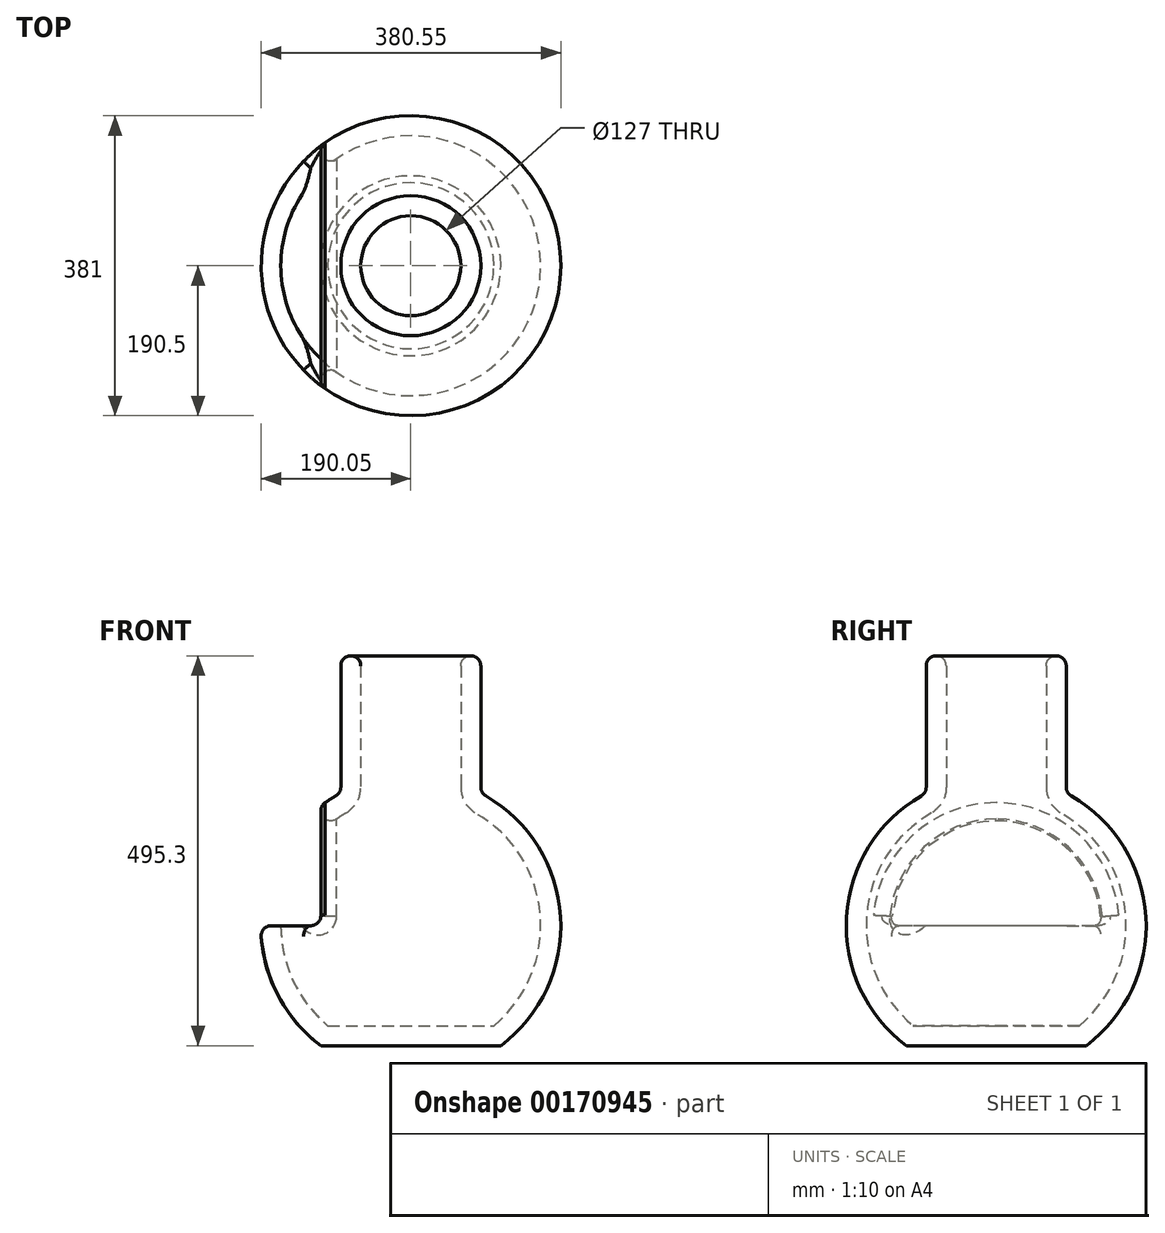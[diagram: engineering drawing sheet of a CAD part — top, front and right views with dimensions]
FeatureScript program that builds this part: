
annotation { "Feature Type Name" : "Feature", "Feature Type Description" : "" }
export const myFeature = defineFeature(function(context is Context, id is Id, definition is map)
    precondition{}
    {
        {
            var Q0;
            Q0=qCreatedBy(makeId("Front.planeOp"),FACE);
            var sketch = newSketch(context, id + "F0", { "sketchPlane" : qUnion([Q0])});
            skArc(sketch, "E0", {"start": v(-95.25, 164.98) * mm, "mid": v(-190.16, 11.41) * mm, "end": v(-114.3, -152.4) * mm});
            skLineSegment(sketch, "E1", {"start": v(0, -152.4) * mm, "end": v(0, 342.9) * mm});
            skLineSegment(sketch, "E2", {"start": v(0, 0) * mm, "end": v(-190.5, 0) * mm});
            skLineSegment(sketch, "E3", {"start": v(0, 342.9) * mm, "end": v(-88.9, 342.9) * mm});
            skLineSegment(sketch, "E4", {"start": v(-88.9, 342.9) * mm, "end": v(-88.9, 175.98) * mm});
            skLineSegment(sketch, "E5", {"start": v(-174.6, -76.2) * mm, "end": v(0, -76.2) * mm});
            skLineSegment(sketch, "E6", {"start": v(0, -152.4) * mm, "end": v(-114.3, -152.4) * mm});
            skLineSegment(sketch, "E7", {"start": v(-174.6, 76.2) * mm, "end": v(0, 76.2) * mm});
            skLineSegment(sketch, "E8", {"start": v(0, 152.4) * mm, "end": v(-114.3, 152.4) * mm});
            skLineSegment(sketch, "E9", {"start": v(-114.3, 152.4) * mm, "end": v(-114.3, 0) * mm});
            skPoint(sketch, "E10.newPointB", {"position": v(0, 190.5) * mm});
            skArc(sketch, "E10.filletArc", {"start": v(-95.25, 164.98) * mm, "mid": v(-90.6, 169.63) * mm, "end": v(-88.9, 175.98) * mm});
            skSolve(sketch);
        }
        {
            var Q0;
            {var subQ4=sQuery(id+"F0.wireOp",EDGE,"E3");Q0=makeQuery(id+"F0.imprint","IMPRINT",FACE,{"disambiguationData":[TD([[makeQuery(id+"F0.imprint","IMPRINT",EDGE,{"derivedFrom":subQ4}),1.0]])]});}
            var Q1;
            {var subQ4=sQuery(id+"F0.wireOp",EDGE,"E8");Q1=makeQuery(id+"F0.imprint","IMPRINT",FACE,{"disambiguationData":[TD([[makeQuery(id+"F0.imprint","IMPRINT",EDGE,{"derivedFrom":subQ4}),-1.0]])]});}
            var Q2;
            {var subQ3=sQuery(id+"F0.wireOp",EDGE,"E8");Q2=makeQuery(id+"F0.imprint","IMPRINT",FACE,{"disambiguationData":[TD([[makeQuery(id+"F0.imprint","IMPRINT",EDGE,{"derivedFrom":subQ3}),1.0]])]});}
            var Q3;
            {var subQ0=sQuery(id+"F0.wireOp",EDGE,"E7");var subQ1=sQuery(id+"F0.wireOp",EDGE,"E0");var subQ2=makeQuery(id+"F0.imprint","INTERSECT",VERTEX,{"derivedFrom":[subQ1,subQ0]});Q3=makeQuery(id+"F0.imprint","IMPRINT",FACE,{"disambiguationData":[TD([[makeQuery(id+"F0.imprint","IMPRINT",EDGE,{"disambiguationData":[TD([[subQ2,-1.0]])],"derivedFrom":subQ0}),1.0]])]});}
            var Q4;
            {var subQ0=sQuery(id+"F0.wireOp",EDGE,"E2");var subQ1=sQuery(id+"F0.wireOp",EDGE,"E0");var subQ2=makeQuery(id+"F0.imprint","INTERSECT",VERTEX,{"derivedFrom":[subQ1,subQ0]});Q4=makeQuery(id+"F0.imprint","IMPRINT",FACE,{"disambiguationData":[TD([[makeQuery(id+"F0.imprint","IMPRINT",EDGE,{"disambiguationData":[TD([[subQ2,1.0]])],"derivedFrom":subQ1}),1.0]])]});}
            var Q5;
            {var subQ0=sQuery(id+"F0.wireOp",EDGE,"E2");var subQ1=sQuery(id+"F0.wireOp",EDGE,"E1");var subQ2=makeQuery(id+"F0.imprint","INTERSECT",VERTEX,{"derivedFrom":[subQ1,subQ0]});Q5=makeQuery(id+"F0.imprint","IMPRINT",FACE,{"disambiguationData":[TD([[makeQuery(id+"F0.imprint","IMPRINT",EDGE,{"disambiguationData":[TD([[subQ2,-1.0]])],"derivedFrom":subQ1}),1.0]])]});}
            var Q6;
            {var subQ6=sQuery(id+"F0.wireOp",EDGE,"E5");Q6=makeQuery(id+"F0.imprint","IMPRINT",FACE,{"disambiguationData":[TD([[makeQuery(id+"F0.imprint","IMPRINT",EDGE,{"derivedFrom":subQ6}),1.0]])]});}
            var Q7;
            {var subQ0=sQuery(id+"F0.wireOp",EDGE,"E5");Q7=makeQuery(id+"F0.imprint","IMPRINT",FACE,{"disambiguationData":[TD([[makeQuery(id+"F0.imprint","IMPRINT",EDGE,{"derivedFrom":subQ0}),-1.0]])]});}
            var Q8;
            Q8=sQuery(id+"F0.wireOp",EDGE,"E1");
            revolve(context, id + "F1", {"entities" : qUnion([Q0, Q1, Q2, Q3, Q4, Q5, Q6, Q7]), "axis" : qUnion([Q8]), "revolveType" : RevolveType.FULL});
        }
        {
            var Q0;
            Q0=makeQuery(id+"F1.opRevolve","SWEPT_FACE",FACE,{"disambiguationData":[OSD([sQuery(id+"F0.wireOp",EDGE,"E3")])]});
            shell(context, id + "F2", {"entities" : qUnion([Q0]), "thickness" : 25.4 * mm});
        }
        {
            var Q0;
            Q0=makeQuery(id+"F1.opRevolve","SWEPT_FACE",FACE,{"disambiguationData":[OSD([sQuery(id+"F0.wireOp",EDGE,"E3")])]});
            fillet(context, id + "F3", {"entities" : qUnion([Q0]), "radius" : 12.7 * mm, "tangentPropagation" : true, "allowEdgeOverflow" : false});
        }
        {
            var Q0;
            {var subQ0=sQuery(id+"F0.wireOp",EDGE,"E7");var subQ1=sQuery(id+"F0.wireOp",EDGE,"E0");var subQ2=makeQuery(id+"F0.imprint","INTERSECT",VERTEX,{"derivedFrom":[subQ1,subQ0]});Q0=makeQuery(id+"F0.imprint","IMPRINT",FACE,{"disambiguationData":[TD([[makeQuery(id+"F0.imprint","IMPRINT",EDGE,{"disambiguationData":[TD([[subQ2,-1.0]])],"derivedFrom":subQ0}),1.0]])]});}
            var Q1;
            {var subQ0=sQuery(id+"F0.wireOp",EDGE,"E2");var subQ1=sQuery(id+"F0.wireOp",EDGE,"E0");var subQ2=makeQuery(id+"F0.imprint","INTERSECT",VERTEX,{"derivedFrom":[subQ1,subQ0]});Q1=makeQuery(id+"F0.imprint","IMPRINT",FACE,{"disambiguationData":[TD([[makeQuery(id+"F0.imprint","IMPRINT",EDGE,{"disambiguationData":[TD([[subQ2,1.0]])],"derivedFrom":subQ1}),1.0]])]});}
            extrude(context, id + "F4", {"entities" : qUnion([Q0, Q1]), "operationType" : NewBodyOperationType.REMOVE, "endBound" : BoundingType.THROUGH_ALL, "oppositeDirection" : true, "depth" : 25.4 * mm, "hasSecondDirection" : true, "secondDirectionOppositeDirection" : false, "secondDirectionDepth" : 181.6 * mm});
        }
        {
            var Q0;
            Q0=makeQuery(id+"F4.boolean.opBoolean","INTERSECT",EDGE,{"derivedFrom":[makeQuery(id+"F1.opRevolve","SWEPT_FACE",FACE,{"disambiguationData":[OSD([sQuery(id+"F0.wireOp",EDGE,"E0")])]}),makeQuery(id+"F4.opExtrude","SWEPT_FACE",FACE,{"disambiguationData":[OSD([sQuery(id+"F0.wireOp",EDGE,"E2")])]})]});
            fillet(context, id + "F5", {"entities" : qUnion([Q0]), "radius" : 12.7 * mm, "tangentPropagation" : true, "allowEdgeOverflow" : false});
        }
        {
            var Q0;
            Q0=makeQuery(id+"F4.boolean.opBoolean","COPY",FACE,{"derivedFrom":makeQuery(id+"F4.opExtrude","SWEPT_FACE",FACE,{"disambiguationData":[OSD([sQuery(id+"F0.wireOp",EDGE,"E9")])]})});
            fillet(context, id + "F6", {"entities" : qUnion([Q0]), "radius" : 12.7 * mm, "tangentPropagation" : true, "allowEdgeOverflow" : false});
        }
    });
